# Revit family: TR3014
name_source: partatom
category: Verbindungsmittel
units: mm (PartAtom-declared; Revit-internal decimal feet)

## family parameters
Arbeitsebenenbasiert = Nein
Beim Laden mit Abzugskörper schneiden = Nein
Gemeinsam genutzt = Nein
Immer vertikal = Nein
OmniClass-Nummer = 23.25.10.27.11.21
OmniClass-Titel = Reinforcement Couplers

## types (10) — shared parameters
Endenbearbeitung 1 = Mit Gewinde
Endenbearbeitung 2 = Mit Gewinde
Hersteller = Stahlwerk Annahütte Max Aicher GmbH Co.KG
Körper = 0,00 kg
Modell = TR 3014
TR3014-L_Vis = Ja
TR3014-SW_Vis = Ja
Typenbild = TR3014.png
Typenkommentare = TR 3014 - Spannmuffe
URL = http//:www.annahuette.com

## per-type parameters (varying)
| type | Außendurchmesser | Beschreibung | Einfassung Stab 1 | Einfassung Stab 2 | Gesamtlänge | Stabgröße 1 | Stabgröße 2 | TR3014-L | TR3014-L1 | TR3014-L2 | TR3014-SW | TR3014-ød |
| TR 3014-ø18 | 41 mm  [stored 0.134514 ft] | TR3014-ø18 | 50 mm  [stored 0.164042 ft] | 45 mm  [stored 0.147638 ft] | 145 mm  [stored 0.475722 ft] | SAS 670 - ø18 | SAS 670 - ø18 | 145 mm  [stored 0.475722 ft] | 50 mm  [stored 0.164042 ft] | 45 mm  [stored 0.147638 ft] | 41 mm  [stored 0.134514 ft] | 18 mm  [stored 0.0590551 ft] |
| TR 3014-ø22 | 46 mm  [stored 0.150919 ft] | TR3014-ø22 | 55 mm  [stored 0.180446 ft] | 50 mm  [stored 0.164042 ft] | 160 mm  [stored 0.524934 ft] | SAS 670 - ø22 | SAS 670 - ø22 | 160 mm  [stored 0.524934 ft] | 55 mm  [stored 0.180446 ft] | 50 mm  [stored 0.164042 ft] | 46 mm  [stored 0.150919 ft] | 22 mm  [stored 0.0721785 ft] |
| TR 3014-ø25 | 55 mm  [stored 0.180446 ft] | TR3014-ø25 | 60 mm  [stored 0.19685 ft] | 55 mm  [stored 0.180446 ft] | 175 mm  [stored 0.574147 ft] | SAS 670 - ø25 | SAS 670 - ø25 | 175 mm  [stored 0.574147 ft] | 60 mm  [stored 0.19685 ft] | 55 mm  [stored 0.180446 ft] | 55 mm  [stored 0.180446 ft] | 25 mm  [stored 0.082021 ft] |
| TR 3014-ø28 | 50 mm  [stored 0.164042 ft] | TR3014-ø28 | 65 mm  [stored 0.213255 ft] | 60 mm  [stored 0.19685 ft] | 190 mm | SAS 670 - ø28 | SAS 670 - ø28 | 190 mm | 65 mm  [stored 0.213255 ft] | 60 mm  [stored 0.19685 ft] | 50 mm  [stored 0.164042 ft] | 28 mm  [stored 0.0918635 ft] |
| TR 3014-ø30 | 65 mm  [stored 0.213255 ft] | TR3014-ø30 | 70 mm  [stored 0.229659 ft] | 65 mm  [stored 0.213255 ft] | 215 mm | SAS 670 - ø30 | SAS 670 - ø30 | 215 mm | 70 mm  [stored 0.229659 ft] | 65 mm  [stored 0.213255 ft] | 65 mm  [stored 0.213255 ft] | 30 mm  [stored 0.0984252 ft] |
| TR 3014-ø35 | 80 mm  [stored 0.262467 ft] | TR3014-ø35 | 75 mm | 75 mm | 230 mm  [stored 0.754593 ft] | SAS 670 - ø35 | SAS 670 - ø35 | 230 mm  [stored 0.754593 ft] | 75 mm | 75 mm | 80 mm  [stored 0.262467 ft] | 35 mm  [stored 0.114829 ft] |
| TR 3014-ø43 | 90 mm  [stored 0.295276 ft] | TR3014-ø43 | 100 mm  [stored 0.328084 ft] | 90 mm  [stored 0.295276 ft] | 280 mm  [stored 0.918635 ft] | SAS 670 - ø43 | SAS 670 - ø43 | 280 mm  [stored 0.918635 ft] | 100 mm  [stored 0.328084 ft] | 90 mm  [stored 0.295276 ft] | 90 mm  [stored 0.295276 ft] | 43 mm  [stored 0.141076 ft] |
| TR 3014-ø50 | 100 mm  [stored 0.328084 ft] | TR3014-ø50 | 100 mm  [stored 0.328084 ft] | 100 mm  [stored 0.328084 ft] | 300 mm | SAS 670 - ø50 | SAS 670 - ø50 | 300 mm | 100 mm  [stored 0.328084 ft] | 100 mm  [stored 0.328084 ft] | 100 mm  [stored 0.328084 ft] | 50 mm  [stored 0.164042 ft] |
| TR 3014-ø57,5 | 100 mm  [stored 0.328084 ft] | TR3014-ø57,5 | 125 mm  [stored 0.410105 ft] | 100 mm  [stored 0.328084 ft] | 345 mm  [stored 1.13189 ft] | SAS 670 - ø57,5 | SAS 670 - ø57,5 | 345 mm  [stored 1.13189 ft] | 125 mm  [stored 0.410105 ft] | 100 mm  [stored 0.328084 ft] | 100 mm  [stored 0.328084 ft] | 58 mm |
| TR 3014-ø63,5 | 100 mm  [stored 0.328084 ft] | TR3014-ø63,5 | 140 mm  [stored 0.459318 ft] | 105 mm  [stored 0.344488 ft] | 365 mm  [stored 1.19751 ft] | SAS 670 - ø63,5 | SAS 670 - ø63,5 | 365 mm  [stored 1.19751 ft] | 140 mm  [stored 0.459318 ft] | 105 mm  [stored 0.344488 ft] | 100 mm  [stored 0.328084 ft] | 43 mm  [stored 0.141076 ft] |

note: [stored X ft] marks values corroborated as IEEE doubles in the binary element streams (Revit-internal decimal feet)
